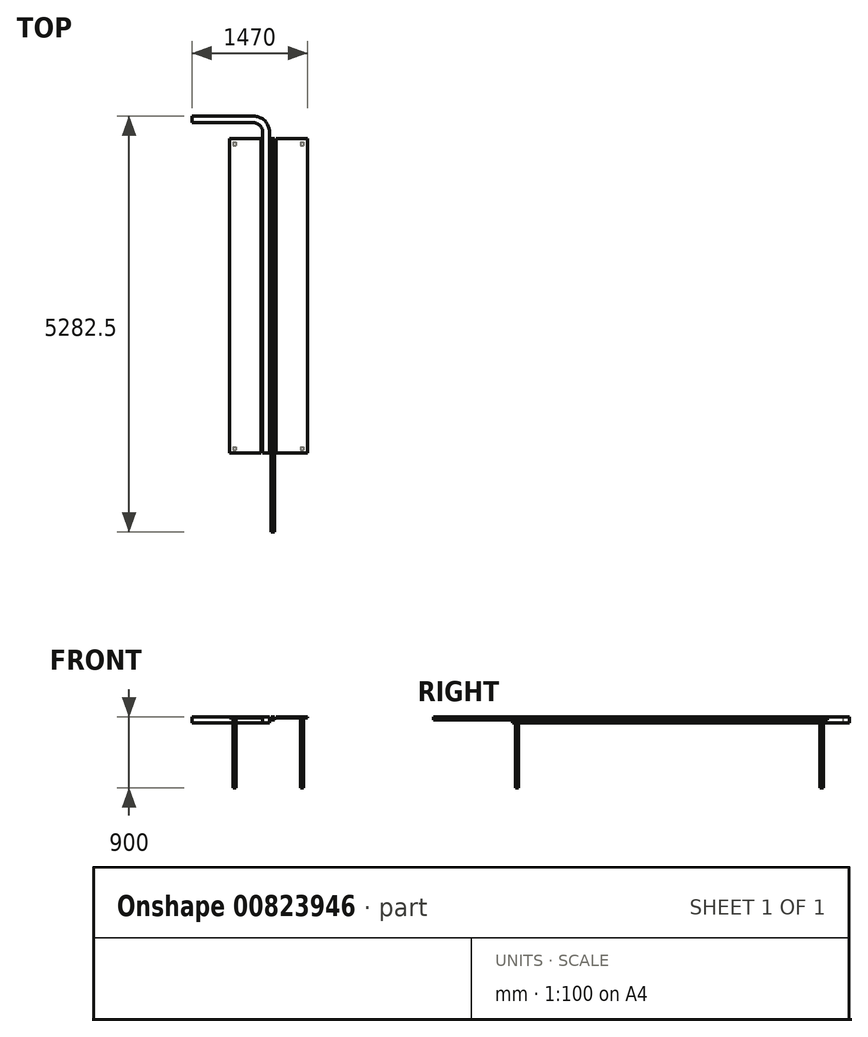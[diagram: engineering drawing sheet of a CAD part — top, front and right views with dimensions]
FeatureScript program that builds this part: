
annotation { "Feature Type Name" : "Feature", "Feature Type Description" : "" }
export const myFeature = defineFeature(function(context is Context, id is Id, definition is map)
    precondition{}
    {
        {
            var Q0;
            Q0=qCreatedBy(makeId("Front.planeOp"),FACE);
            var sketch = newSketch(context, id + "F0", { "sketchPlane" : qUnion([Q0])});
            skLineSegment(sketch, "E0.bottom", {"start": v(0, 0) * mm, "end": v(45, 0) * mm});
            skLineSegment(sketch, "E0.top", {"start": v(0, 41) * mm, "end": v(45, 41) * mm});
            skLineSegment(sketch, "E0.left", {"start": v(0, 0) * mm, "end": v(0, 41) * mm});
            skLineSegment(sketch, "E0.right", {"start": v(45, 0) * mm, "end": v(45, 41) * mm});
            skSolve(sketch);
        }
        {
            var Q0;
            Q0=makeQuery(id+"F0.imprint","IMPRINT",FACE,{"disambiguationData":[TD([[makeQuery(id+"F0.imprint","IMPRINT",EDGE,{"derivedFrom":sQuery(id+"F0.wireOp",EDGE,"E0.bottom")}),1.0]])]});
            extrude(context, id + "F1", {"entities" : qUnion([Q0]), "oppositeDirection" : true, "depth" : 5000 * mm, "offsetDistance" : 25 * mm});
        }
        {
            var Q0;
            Q0=qCreatedBy(makeId("Front.planeOp"),FACE);
            cPlane(context, id + "F2", {"entities" : qUnion([Q0]), "cplaneType" : CPlaneType.OFFSET, "offset" : 1000 * mm, "oppositeDirection" : true, "width" : 150 * mm, "height" : 150 * mm});
        }
        {
            var Q0;
            Q0=qCreatedBy(id+"F2.planeOp",FACE);
            var sketch = newSketch(context, id + "F3", { "sketchPlane" : qUnion([Q0])});
            skPoint(sketch, "E1.0", {"position": v(0, 41) * mm});
            skLineSegment(sketch, "E2.bottom", {"start": v(-20, 41) * mm, "end": v(-105, 41) * mm});
            skLineSegment(sketch, "E2.top", {"start": v(-20, -33) * mm, "end": v(-105, -33) * mm});
            skLineSegment(sketch, "E2.left", {"start": v(-20, 41) * mm, "end": v(-20, -33) * mm});
            skLineSegment(sketch, "E2.right", {"start": v(-105, 41) * mm, "end": v(-105, -33) * mm});
            skSolve(sketch);
        }
        {
            var Q0;
            Q0=makeQuery(id+"F3.imprint","IMPRINT",FACE,{"disambiguationData":[TD([[makeQuery(id+"F3.imprint","IMPRINT",EDGE,{"derivedFrom":sQuery(id+"F3.wireOp",EDGE,"E2.bottom")}),1.0]])]});
            extrude(context, id + "F4", {"entities" : qUnion([Q0]), "oppositeDirection" : true, "depth" : 4080 * mm, "offsetDistance" : 25 * mm});
        }
        {
            var Q0;
            Q0=makeQuery(id+"F4.opExtrude","CAP_FACE",FACE,{"disambiguationData":[OSD([sQuery(id+"F3.wireOp",EDGE,"E2.bottom"),sQuery(id+"F3.wireOp",EDGE,"E2.top"),sQuery(id+"F3.wireOp",EDGE,"E2.left"),sQuery(id+"F3.wireOp",EDGE,"E2.right")])],"isStart":false});
            var sketch = newSketch(context, id + "F5", { "sketchPlane" : qUnion([Q0])});
            skLineSegment(sketch, "E3.0.0", {"start": v(20, -33) * mm, "end": v(105, -33) * mm});
            skLineSegment(sketch, "E3.0.1", {"start": v(105, -33) * mm, "end": v(105, 41) * mm});
            skLineSegment(sketch, "E3.0.2", {"start": v(105, 41) * mm, "end": v(20, 41) * mm});
            skLineSegment(sketch, "E3.0.3", {"start": v(20, 41) * mm, "end": v(20, -33) * mm});
            skLineSegment(sketch, "E4", {"start": v(222.5, 51.73) * mm, "end": v(222.5, -29.32) * mm, "construction": true});
            skLineSegment(sketch, "E5", {"start": v(62.5, 41) * mm, "end": v(62.5, -33) * mm, "construction": true});
            skSolve(sketch);
        }
        {
            var Q0;
            Q0=makeQuery(id+"F5.imprint","IMPRINT",FACE,{"disambiguationData":[TD([[makeQuery(id+"F5.imprint","IMPRINT",EDGE,{"derivedFrom":sQuery(id+"F5.wireOp",EDGE,"E3.0.0")}),1.0]])]});
            var Q1;
            Q1=sQuery(id+"F5.wireOp",EDGE,"E4");
            revolve(context, id + "F6", {"operationType" : NewBodyOperationType.ADD, "surfaceOperationType" : NewSurfaceOperationType.NEW, "entities" : qUnion([Q0]), "axis" : qUnion([Q1]), "revolveType" : RevolveType.ONE_DIRECTION, "oppositeDirection" : true, "angle" : 90 * degree});
        }
        {
            var Q0;
            Q0=makeQuery(id+"F6.opRevolve","CAP_FACE",FACE,{"disambiguationData":[OSD([sQuery(id+"F5.wireOp",EDGE,"E3.0.0"),sQuery(id+"F5.wireOp",EDGE,"E3.0.1"),sQuery(id+"F5.wireOp",EDGE,"E3.0.2"),sQuery(id+"F5.wireOp",EDGE,"E3.0.3")])],"isStart":false});
            var sketch = newSketch(context, id + "F7", { "sketchPlane" : qUnion([Q0])});
            skLineSegment(sketch, "E6.0.0", {"start": v(-5282.5, 41) * mm, "end": v(-5282.5, -33) * mm});
            skLineSegment(sketch, "E6.0.1", {"start": v(-5282.5, -33) * mm, "end": v(-5197.5, -33) * mm});
            skLineSegment(sketch, "E6.0.2", {"start": v(-5197.5, -33) * mm, "end": v(-5197.5, 41) * mm});
            skLineSegment(sketch, "E6.0.3", {"start": v(-5197.5, 41) * mm, "end": v(-5282.5, 41) * mm});
            skSolve(sketch);
        }
        {
            var Q0;
            Q0=makeQuery(id+"F7.imprint","IMPRINT",FACE,{"disambiguationData":[TD([[makeQuery(id+"F7.imprint","IMPRINT",EDGE,{"derivedFrom":sQuery(id+"F7.wireOp",EDGE,"E6.0.0")}),1.0]])]});
            extrude(context, id + "F8", {"entities" : qUnion([Q0]), "operationType" : NewBodyOperationType.ADD, "depth" : 782.5 * mm, "offsetDistance" : 25 * mm});
        }
        {
            var Q0;
            Q0=makeQuery(id+"F8.boolean.opBoolean","MERGE",FACE,{"derivedFrom":[makeQuery(id+"F6.boolean.opBoolean","MERGE",FACE,{"derivedFrom":[makeQuery(id+"F4.opExtrude","SWEPT_FACE",FACE,{"disambiguationData":[OSD([sQuery(id+"F3.wireOp",EDGE,"E2.bottom")])]}),makeQuery(id+"F6.opRevolve","SWEPT_FACE",FACE,{"disambiguationData":[OSD([sQuery(id+"F5.wireOp",EDGE,"E3.0.2")])]})]}),makeQuery(id+"F8.opExtrude","SWEPT_FACE",FACE,{"disambiguationData":[OSD([sQuery(id+"F7.wireOp",EDGE,"E6.0.3")])]})]});
            var sketch = newSketch(context, id + "F9", { "sketchPlane" : qUnion([Q0])});
            skLineSegment(sketch, "E7.bottom", {"start": v(-125, 1000) * mm, "end": v(-525, 1000) * mm});
            skLineSegment(sketch, "E7.top", {"start": v(-125, 5000) * mm, "end": v(-525, 5000) * mm});
            skLineSegment(sketch, "E7.left", {"start": v(-125, 1000) * mm, "end": v(-125, 5000) * mm});
            skLineSegment(sketch, "E7.right", {"start": v(-525, 1000) * mm, "end": v(-525, 5000) * mm});
            skLineSegment(sketch, "E8.bottom", {"start": v(65, 1000) * mm, "end": v(465, 1000) * mm});
            skLineSegment(sketch, "E8.top", {"start": v(65, 5000) * mm, "end": v(465, 5000) * mm});
            skLineSegment(sketch, "E8.left", {"start": v(65, 1000) * mm, "end": v(65, 5000) * mm});
            skLineSegment(sketch, "E8.right", {"start": v(465, 1000) * mm, "end": v(465, 5000) * mm});
            skSolve(sketch);
        }
        {
            var Q0;
            Q0=makeQuery(id+"F9.imprint","IMPRINT",FACE,{"disambiguationData":[TD([[makeQuery(id+"F9.imprint","IMPRINT",EDGE,{"derivedFrom":sQuery(id+"F9.wireOp",EDGE,"E7.bottom")}),-1.0]])]});
            var Q1;
            Q1=makeQuery(id+"F9.imprint","IMPRINT",FACE,{"disambiguationData":[TD([[makeQuery(id+"F9.imprint","IMPRINT",EDGE,{"derivedFrom":sQuery(id+"F9.wireOp",EDGE,"E8.bottom")}),1.0]])]});
            extrude(context, id + "F10", {"entities" : qUnion([Q0, Q1]), "oppositeDirection" : true, "depth" : 10 * mm, "offsetDistance" : 25 * mm});
        }
        {
            var Q0;
            Q0=makeQuery(id+"F10.opExtrude","CAP_FACE",FACE,{"disambiguationData":[OSD([sQuery(id+"F9.wireOp",EDGE,"E7.bottom"),sQuery(id+"F9.wireOp",EDGE,"E7.top"),sQuery(id+"F9.wireOp",EDGE,"E7.left"),sQuery(id+"F9.wireOp",EDGE,"E7.right")])],"isStart":false});
            var sketch = newSketch(context, id + "F11", { "sketchPlane" : qUnion([Q0])});
            skLineSegment(sketch, "E9.bottom", {"start": v(-485, -4950) * mm, "end": v(-445, -4950) * mm});
            skLineSegment(sketch, "E9.top", {"start": v(-485, -4910) * mm, "end": v(-445, -4910) * mm});
            skLineSegment(sketch, "E9.left", {"start": v(-485, -4950) * mm, "end": v(-485, -4910) * mm});
            skLineSegment(sketch, "E9.right", {"start": v(-445, -4950) * mm, "end": v(-445, -4910) * mm});
            skLineSegment(sketch, "E10.bottom", {"start": v(375, -4950) * mm, "end": v(415, -4950) * mm});
            skLineSegment(sketch, "E10.top", {"start": v(375, -4910) * mm, "end": v(415, -4910) * mm});
            skLineSegment(sketch, "E10.left", {"start": v(375, -4950) * mm, "end": v(375, -4910) * mm});
            skLineSegment(sketch, "E10.right", {"start": v(415, -4950) * mm, "end": v(415, -4910) * mm});
            skLineSegment(sketch, "E11.bottom", {"start": v(-485, -1080) * mm, "end": v(-445, -1080) * mm});
            skLineSegment(sketch, "E11.top", {"start": v(-485, -1040) * mm, "end": v(-445, -1040) * mm});
            skLineSegment(sketch, "E11.left", {"start": v(-485, -1080) * mm, "end": v(-485, -1040) * mm});
            skLineSegment(sketch, "E11.right", {"start": v(-445, -1080) * mm, "end": v(-445, -1040) * mm});
            skLineSegment(sketch, "E12.bottom", {"start": v(375, -1080) * mm, "end": v(415, -1080) * mm});
            skLineSegment(sketch, "E12.top", {"start": v(375, -1040) * mm, "end": v(415, -1040) * mm});
            skLineSegment(sketch, "E12.left", {"start": v(375, -1080) * mm, "end": v(375, -1040) * mm});
            skLineSegment(sketch, "E12.right", {"start": v(415, -1080) * mm, "end": v(415, -1040) * mm});
            skSolve(sketch);
        }
        {
            var Q0;
            Q0=makeQuery(id+"F11.imprint","IMPRINT",FACE,{"disambiguationData":[TD([[makeQuery(id+"F11.imprint","IMPRINT",EDGE,{"derivedFrom":sQuery(id+"F11.wireOp",EDGE,"E9.bottom")}),1.0]])]});
            var Q1;
            Q1=makeQuery(id+"F11.imprint","IMPRINT",FACE,{"disambiguationData":[TD([[makeQuery(id+"F11.imprint","IMPRINT",EDGE,{"derivedFrom":sQuery(id+"F11.wireOp",EDGE,"E10.bottom")}),1.0]])]});
            var Q2;
            Q2=makeQuery(id+"F11.imprint","IMPRINT",FACE,{"disambiguationData":[TD([[makeQuery(id+"F11.imprint","IMPRINT",EDGE,{"derivedFrom":sQuery(id+"F11.wireOp",EDGE,"E12.bottom")}),1.0]])]});
            var Q3;
            Q3=makeQuery(id+"F11.imprint","IMPRINT",FACE,{"disambiguationData":[TD([[makeQuery(id+"F11.imprint","IMPRINT",EDGE,{"derivedFrom":sQuery(id+"F11.wireOp",EDGE,"E11.bottom")}),1.0]])]});
            extrude(context, id + "F12", {"entities" : qUnion([Q0, Q1, Q2, Q3]), "depth" : 890 * mm, "offsetDistance" : 25 * mm});
        }
    });
